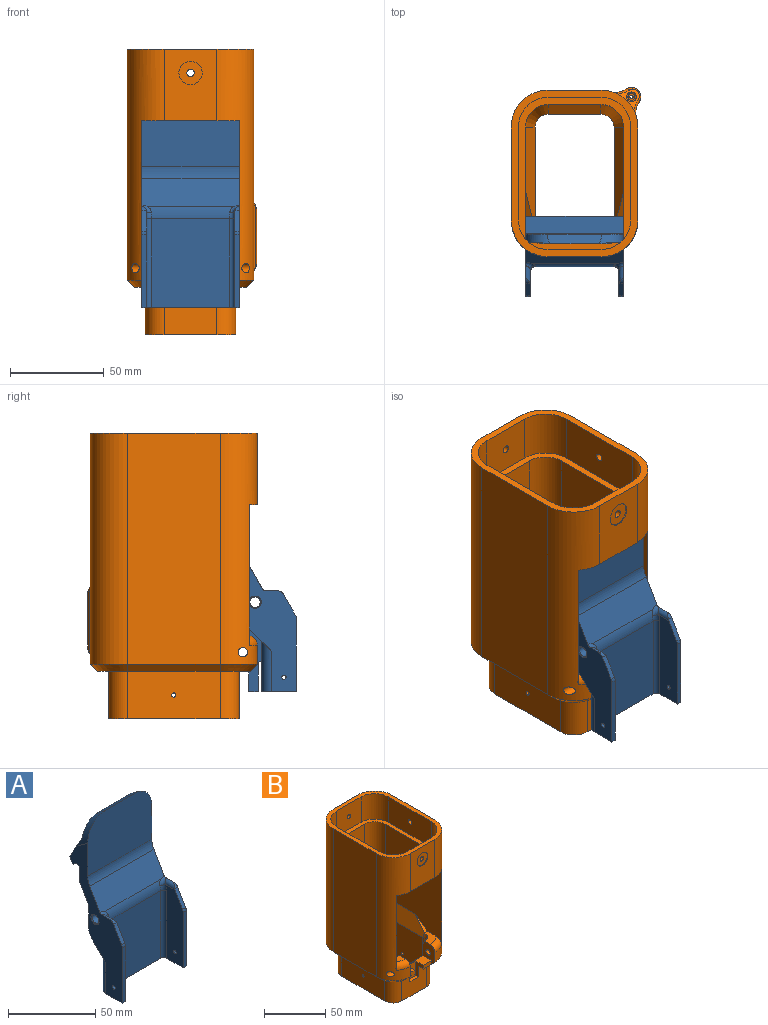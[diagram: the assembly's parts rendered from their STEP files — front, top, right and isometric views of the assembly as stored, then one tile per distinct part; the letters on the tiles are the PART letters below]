
ASSEMBLY  parts=2 mates=1
PART A: 74 faces, bbox 55.6x46.3x116.4 mm
  f0: cylinder r=5.71mm len=7.94mm, axis (-1,0,0), area 71.3mm2, adj f1,f14,f40,f43
  f1: plane 25.4x2.96mm, normal (0,1,0), area 48.8mm2, adj f0,f3,f16,f29,f40,f43,f44,f73
  f2: plane 25.4x4.95mm, normal (0,0,-1), area 110.7mm2, adj f3,f13,f23,f40,f43,f44,f46,f62
  f3: plane 39.51x15.88mm, normal (1,0,0), area 282.7mm2, adj f1,f2,f16,f23,f24,f25,f26,f27
  f4: plane 98.14x42.62mm, normal (1,0,0), area 1360.4mm2, adj f7,f17,f18,f22,f28,f30,f31,f32
  f5: plane 98.14x42.62mm, normal (-1,0,0), area 1360.4mm2, adj f8,f10,f17,f18,f22,f28,f30,f31
  f6: plane 51.21x13.82mm, normal (-1,0,0), area 642.1mm2, adj f7,f17,f49,f50,f51,f59,f61,f67
  f7: cylinder r=2.54mm len=9.64mm, axis (0,1,0), area 26.8mm2, adj f4,f6,f52,f60,f61
  f8: plane 38.82x2.54mm, normal (0,-1,0), area 98.6mm2, adj f5,f9,f17,f58
  f9: plane 51.21x13.82mm, normal (1,0,0), area 642.1mm2, adj f8,f10,f17,f53,f54,f56,f58,f66
  f10: cylinder r=2.54mm len=9.64mm, axis (0,-1,0), area 26.8mm2, adj f5,f9,f55,f56,f57
  f11: plane 47.4x41.91mm, normal (0,-1,0), area 1986.4mm2, adj f12,f17,f50,f53
  f12: cylinder r=12.7mm len=45.35mm, axis (-1,0,0), area 284.6mm2, adj f11,f30,f51,f52,f54,f55
  f13: plane 12.07x7.94mm, normal (0,1,0), area 95.8mm2, adj f2,f14,f40,f43
  f14: cylinder r=3.17mm len=7.94mm, axis (-1,0,0), area 39.6mm2, adj f0,f13,f40,f43
  f15: cylinder r=2.6mm len=7.94mm, axis (-1,0,0), area 129.8mm2, adj f40,f43
  f16: cylinder r=5.71mm len=7.94mm, axis (-1,0,0), area 71.3mm2, adj f1,f3,f24,f44
  f17: plane 52.07x18.42mm, normal (0,0,-1), area 204.6mm2, adj f4,f5,f6,f8,f9,f11,f38,f49
  f18: plane 52.1x15.43mm, normal (0,0.87,0.5), area 925.3mm2, adj f4,f5,f19,f36,f41,f42
  f19: cylinder r=5.08mm len=51.58mm, axis (-1,0,0), area 136mm2, adj f18,f20,f41,f42
  f20: plane 52.71x12.86mm, normal (0,1,0), area 478.1mm2, adj f19,f21,f41,f42
  f21: plane 29.57x5.08mm, normal (0,0.59,0.81), area 177mm2, adj f20,f22,f41,f42
  f22: plane 52.07x39.2mm, normal (0,-1,0), area 1948.5mm2, adj f4,f5,f21,f41,f42,f47
  f23: plane 12.07x7.94mm, normal (0,1,0), area 95.8mm2, adj f2,f3,f24,f44
  f24: cylinder r=3.17mm len=7.94mm, axis (-1,0,0), area 39.6mm2, adj f3,f16,f23,f44
  f25: plane 25.4x5.62mm, normal (0,0.64,0.77), area 186.5mm2, adj f3,f26,f29,f40
  f26: cylinder r=0.64mm len=25.4mm, axis (-1,0,0), area 14.1mm2, adj f3,f25,f28,f40
  f27: cylinder r=2.6mm len=7.94mm, axis (-1,0,0), area 129.8mm2, adj f3,f44
  f28: plane 52.07x23.8mm, normal (0,1,0), area 1027.3mm2, adj f3,f4,f5,f26,f31,f40,f70,f71
  f29: cylinder r=3.17mm len=25.4mm, axis (-1,0,0), area 70.4mm2, adj f1,f3,f25,f40
  f30: plane 52.23x15.16mm, normal (0,-0.87,0.5), area 898mm2, adj f4,f5,f12,f47,f52,f55
  f31: plane 52.07x12.1mm, normal (0,0.87,-0.5), area 727.4mm2, adj f4,f5,f28,f32
  f32: plane 52.07x9.48mm, normal (0,1,0), area 493.6mm2, adj f4,f5,f31,f33
  f33: cylinder r=2.54mm len=52.07mm, axis (-1,0,0), area 346.3mm2, adj f4,f5,f32,f34
  f34: plane 52.07x0.13mm, normal (0,-0.87,-0.5), area 7.6mm2, adj f4,f5,f33,f35
  f35: cylinder r=0.76mm len=52.07mm, axis (-1,0,0), area 83.1mm2, adj f4,f5,f34,f36
  f36: plane 52.07x3.76mm, normal (0,0.87,-0.5), area 226.2mm2, adj f4,f5,f18,f35
  f37: plane 15.47x13.32mm, normal (0,0.71,-0.71), area 122.9mm2, adj f3,f4,f38,f64,f71
  f38: plane 41.91x26.67mm, normal (0,1,0), area 817.7mm2, adj f3,f17,f37,f39,f40,f63,f64,f65
  f39: plane 15.47x13.32mm, normal (0,0.71,-0.71), area 122.9mm2, adj f5,f38,f40,f63,f70
  f40: plane 39.51x15.88mm, normal (-1,0,0), area 282.7mm2, adj f0,f1,f2,f13,f14,f15,f25,f26
  f41: cylinder r=13.33mm len=23.82mm, axis (0,-0.82,0.57), area 137.7mm2, adj f4,f18,f19,f20,f21,f22
  f42: cylinder r=13.33mm len=23.82mm, axis (0,-0.82,0.57), area 137.7mm2, adj f5,f18,f19,f20,f21,f22
  f43: plane 25.72x10.48mm, normal (1,0,0), area 96.4mm2, adj f0,f1,f2,f13,f14,f15,f45,f46
  f44: plane 25.72x10.48mm, normal (-1,0,0), area 96.4mm2, adj f1,f2,f16,f23,f24,f27,f45,f46
  f45: cylinder r=4.76mm len=9.53mm, axis (1,0,0), area 102.9mm2, adj f43,f44,f46,f72
  f46: plane 20.96x9.53mm, normal (0,1,0), area 199.6mm2, adj f2,f43,f44,f45
  f47: cylinder r=12.7mm len=52.07mm, axis (-1,0,0), area 346.3mm2, adj f4,f5,f22,f30
  f48: cylinder r=2.78mm len=51.05mm, axis (1,0,0), area 891.3mm2, adj f68,f69
  f49: plane 38.82x2.54mm, normal (0,-1,0), area 98.6mm2, adj f4,f6,f17,f59
  f50: cylinder r=2.54mm len=47.4mm, axis (0,0,1), area 189.1mm2, adj f6,f11,f17,f51
  f51: torus R=15.24mm, axis (1,0,0), area 13.7mm2, adj f6,f12,f50,f52
  f52: bspline ~5.75x5.23mm, area 17.1mm2, adj f4,f7,f12,f30,f51
  f53: cylinder r=2.54mm len=47.4mm, axis (0,0,1), area 189.1mm2, adj f9,f11,f17,f54
  f54: torus R=15.24mm, axis (-1,0,0), area 13.7mm2, adj f9,f12,f53,f55
  f55: bspline ~5.75x5.23mm, area 17.1mm2, adj f5,f10,f12,f30,f54
  f56: plane 11.12x6.42mm, normal (0,-0.87,0.5), area 32.6mm2, adj f5,f9,f10,f57,f58
  f57: cylinder r=3.81mm len=3.3mm, axis (1,0,0), area 4.9mm2, adj f5,f10,f56
  f58: cylinder r=3.81mm len=2.54mm, axis (1,0,0), area 5.1mm2, adj f5,f8,f9,f56
  f59: cylinder r=3.81mm len=2.54mm, axis (1,0,0), area 5.1mm2, adj f4,f6,f49,f61
  f60: cylinder r=3.81mm len=3.3mm, axis (1,0,0), area 4.9mm2, adj f4,f7,f61
  f61: plane 11.12x6.42mm, normal (0,-0.87,0.5), area 32.6mm2, adj f4,f6,f7,f59,f60
  f62: plane 25.4x14.86mm, normal (0,-1,0), area 377.4mm2, adj f2,f3,f40,f65
  f63: cylinder r=5.08mm len=26.67mm, axis (0,0,-1), area 192.5mm2, adj f5,f17,f38,f39
  f64: cylinder r=5.08mm len=26.67mm, axis (0,0,1), area 192.5mm2, adj f4,f17,f37,f38
  f65: cylinder r=1.02mm len=25.4mm, axis (1,0,0), area 81.1mm2, adj f3,f38,f40,f62
  f66: cylinder r=1.13mm len=2.54mm, axis (1,0,0), area 18mm2, adj f5,f9
  f67: cylinder r=1.13mm len=2.54mm, axis (1,0,0), area 18mm2, adj f4,f6
  f68: cone r=2.78mm half-angle=45deg, axis (-1,0,0), area 13.7mm2, adj f5,f48
  f69: cone r=2.78mm half-angle=45deg, axis (1,0,0), area 13.7mm2, adj f4,f48
  f70: cylinder r=9.53mm len=13.34mm, axis (-1,0,0), area 99.8mm2, adj f5,f28,f39,f40
  f71: cylinder r=9.53mm len=13.34mm, axis (-1,0,0), area 99.8mm2, adj f3,f4,f28,f37
  f72: plane 9.53x1.61mm, normal (0,-0.64,-0.77), area 20mm2, adj f43,f44,f45,f73
  f73: cylinder r=0.64mm len=9.53mm, axis (-1,0,0), area 13.7mm2, adj f1,f43,f44,f72
PART B: 104 faces, bbox 75.7x98.6x155.2 mm
  f0: cylinder r=19.69mm len=123.19mm, axis (0,0,-1), area 2900mm2, adj f14,f17,f26,f59,f77,f79,f84,f85
  f1: plane 28.19x9.65mm, normal (0,0,1), area 190.5mm2, adj f4,f36,f66,f67,f68,f73,f74,f75
  f2: plane 28.19x25.4mm, normal (0,-1,0), area 613.3mm2, adj f3,f27,f48,f54,f74,f75,f76
  f3: plane 81.28x59.94mm, normal (0,0,-1), area 1328mm2, adj f2,f4,f48,f49,f50,f51,f52,f53
  f4: plane 9.33x3.81mm, normal (0,-1,0), area 35.6mm2, adj f1,f3,f66,f74
  f5: plane 52.32x7.62mm, normal (0,0,-1), area 367mm2, adj f10,f11,f12,f13,f29,f30
  f6: plane 75.72x59.94mm, normal (0,0,1), area 705.9mm2, adj f18,f19,f20,f22,f23,f24,f25,f28
  f7: plane 48.83x3.81mm, normal (0,0,1), area 161.2mm2, adj f13,f20,f21,f22
  f8: plane 15.37x12.07mm, normal (0,0,1), area 107.5mm2, adj f29,f41,f63,f66,f71
  f9: cylinder r=2.5mm len=17.21mm, axis (1,0,0), area 241.7mm2, adj f11,f67
  f10: cylinder r=19.69mm len=123.19mm, axis (0,0,-1), area 2811mm2, adj f5,f12,f16,f26,f29,f56,f65,f66
  f11: cylinder r=19.69mm len=123.19mm, axis (0,0,-1), area 2811mm2, adj f5,f9,f12,f17,f26,f30,f55,f67
  f12: plane 38.1x28.19mm, normal (0,-1,0), area 952.5mm2, adj f5,f10,f11,f26,f97
  f13: plane 52.32x12.7mm, normal (0,1,0), area 664.5mm2, adj f5,f7,f29,f30,f69,f70
  f14: plane 123.19x28.19mm, normal (0,1,0), area 3351.6mm2, adj f0,f15,f26,f61,f100
  f15: cylinder r=19.69mm len=123.19mm, axis (0,0,-1), area 3809.2mm2, adj f14,f16,f26,f60
  f16: plane 123.19x49.53mm, normal (-1,0,0), area 6101.6mm2, adj f10,f15,f26,f58
  f17: plane 123.19x49.53mm, normal (1,0,0), area 5979.9mm2, adj f0,f11,f26,f57,f92
  f18: cylinder r=15.88mm len=25.4mm, axis (0,0,-1), area 633.4mm2, adj f6,f19,f25,f26
  f19: plane 49.53x25.4mm, normal (-1,0,0), area 1245.7mm2, adj f6,f18,f20,f26,f94
  f20: cylinder r=15.88mm len=25.4mm, axis (0,0,-1), area 633.4mm2, adj f6,f7,f19,f21,f26,f70
  f21: plane 28.19x25.4mm, normal (0,1,0), area 703.8mm2, adj f7,f20,f22,f26,f95
  f22: cylinder r=15.88mm len=25.4mm, axis (0,0,-1), area 633.4mm2, adj f6,f7,f21,f23,f26,f69
  f23: plane 49.53x25.4mm, normal (1,0,0), area 1258.1mm2, adj f6,f22,f24,f26
  f24: cylinder r=15.88mm len=25.4mm, axis (0,0,-1), area 633.4mm2, adj f6,f23,f25,f26
  f25: plane 28.19x25.4mm, normal (0,-1,0), area 703.8mm2, adj f6,f18,f24,f26,f98
  f26: plane 88.9x67.56mm, normal (0,0,1), area 1017.9mm2, adj f0,f10,f11,f12,f14,f15,f16,f17
  f27: plane 69.6x48.26mm, normal (0,0,-1), area 668.9mm2, adj f2,f33,f34,f35,f36,f37,f38,f39
  f28: cylinder r=12.06mm len=72.4mm, axis (0,0,1), area 1372.2mm2, adj f6,f29,f32,f45
  f29: plane 90.39x67.85mm, normal (1,0,0), area 4914.4mm2, adj f5,f6,f8,f10,f13,f28,f43,f63
  f30: plane 90.39x67.85mm, normal (-1,0,0), area 4914.4mm2, adj f5,f6,f11,f13,f31,f44,f62,f64
  f31: cylinder r=12.06mm len=72.4mm, axis (0,0,1), area 1372.2mm2, adj f6,f30,f32,f46
  f32: plane 72.4x28.19mm, normal (0,-1,0), area 2041.3mm2, adj f6,f28,f31,f47
  f33: cylinder r=6.99mm len=40.64mm, axis (0,0,-1), area 445.9mm2, adj f27,f34,f38,f46
  f34: plane 48.77x40.64mm, normal (-1,0,0), area 1977.9mm2, adj f27,f33,f35,f44,f102
  f35: cylinder r=6.99mm len=40.64mm, axis (0,0,-1), area 445.9mm2, adj f27,f34,f36,f42,f67
  f36: plane 29.21x28.19mm, normal (0,1,0), area 823.5mm2, adj f1,f27,f35,f37
  f37: cylinder r=6.99mm len=40.64mm, axis (0,0,-1), area 445.9mm2, adj f27,f36,f39,f41,f66
  f38: plane 40.64x28.19mm, normal (0,-1,0), area 1141.8mm2, adj f27,f33,f40,f47,f103
  f39: plane 48.77x40.64mm, normal (1,0,0), area 1977.9mm2, adj f27,f37,f40,f43,f101
  f40: cylinder r=6.99mm len=40.64mm, axis (0,0,-1), area 445.9mm2, adj f27,f38,f39,f45
  f41: cone r=6.99mm half-angle=20deg, axis (0,0,1), area 48.9mm2, adj f8,f37,f43,f66
  f42: cone r=6.99mm half-angle=20deg, axis (0,0,1), area 48.9mm2, adj f35,f44,f62,f67
  f43: plane 48.77x13.96mm, normal (0.94,0,0.34), area 646.1mm2, adj f29,f39,f41,f45,f63
  f44: plane 48.77x13.96mm, normal (-0.94,0,0.34), area 646.1mm2, adj f30,f34,f42,f46,f64
  f45: cone r=15.31mm half-angle=20deg, axis (0,0,1), area 222.2mm2, adj f28,f40,f43,f47
  f46: cone r=15.31mm half-angle=20deg, axis (0,0,1), area 222.2mm2, adj f31,f33,f44,f47
  f47: plane 28.19x13.96mm, normal (0,-0.94,0.34), area 418.8mm2, adj f32,f38,f45,f46
  f48: cylinder r=10.03mm len=25.4mm, axis (0,0,-1), area 400.3mm2, adj f2,f3,f27,f49
  f49: plane 49.53x25.4mm, normal (1,0,0), area 1254mm2, adj f3,f27,f48,f50,f102
  f50: cylinder r=10.03mm len=25.4mm, axis (0,0,-1), area 400.3mm2, adj f3,f27,f49,f51
  f51: plane 28.19x25.4mm, normal (0,1,0), area 712.1mm2, adj f3,f27,f50,f52,f103
  f52: cylinder r=10.03mm len=25.4mm, axis (0,0,-1), area 400.3mm2, adj f3,f27,f51,f53
  f53: plane 49.53x25.4mm, normal (-1,0,0), area 1254mm2, adj f3,f27,f52,f54,f101
  f54: cylinder r=10.03mm len=25.4mm, axis (0,0,-1), area 400.3mm2, adj f2,f3,f27,f53
  f55: cone r=19.69mm half-angle=45deg, axis (0,0,1), area 150.5mm2, adj f3,f11,f57,f67
  f56: cone r=19.69mm half-angle=45deg, axis (0,0,1), area 150.5mm2, adj f3,f10,f58,f66
  f57: plane 49.53x3.81mm, normal (0.71,0,-0.71), area 266.9mm2, adj f3,f17,f55,f59
  f58: plane 49.53x3.81mm, normal (-0.71,0,-0.71), area 266.9mm2, adj f3,f16,f56,f60
  f59: cone r=19.69mm half-angle=45deg, axis (0,0,1), area 150.5mm2, adj f0,f3,f57,f61
  f60: cone r=19.69mm half-angle=45deg, axis (0,0,1), area 150.5mm2, adj f3,f15,f58,f61
  f61: plane 28.19x3.81mm, normal (0,0.71,-0.71), area 151.9mm2, adj f3,f14,f59,f60
  f62: plane 15.37x12.07mm, normal (0,0,1), area 107.5mm2, adj f30,f42,f64,f67,f72
  f63: plane 14.49x10.15mm, normal (0,-0.57,0.82), area 32.7mm2, adj f8,f29,f43
  f64: plane 14.49x10.15mm, normal (0,-0.57,0.82), area 32.7mm2, adj f30,f44,f62
  f65: cylinder r=2.5mm len=17.21mm, axis (1,0,0), area 241.8mm2, adj f10,f66
  f66: plane 19.05x13.46mm, normal (1,0,0), area 184.6mm2, adj f1,f4,f8,f10,f37,f41,f56,f65
  f67: plane 19.05x13.46mm, normal (-1,0,0), area 184.6mm2, adj f1,f9,f11,f35,f42,f55,f62,f68
  f68: plane 9.33x3.81mm, normal (0,-1,0), area 35.6mm2, adj f1,f3,f67,f75
  f69: plane 1.75x1.75mm, normal (0,0,-1), area 1.4mm2, adj f13,f22,f29
  f70: plane 1.75x1.75mm, normal (0,0,-1), area 1.4mm2, adj f13,f20,f30
  f71: torus R=14.61mm, axis (0,0,-1), area 115mm2, adj f8,f10,f29,f66
  f72: torus R=14.61mm, axis (0,0,-1), area 115mm2, adj f11,f30,f62,f67
  f73: plane 14.61x9.53mm, normal (0,-1,0), area 139.1mm2, adj f1,f74,f75,f76
  f74: plane 14.61x8.57mm, normal (1,0,0), area 62.1mm2, adj f1,f2,f3,f4,f73,f76
  f75: plane 14.61x8.57mm, normal (-1,0,0), area 62.1mm2, adj f1,f2,f3,f68,f73,f76
  f76: plane 9.53x2.73mm, normal (0,0,1), area 26mm2, adj f2,f73,f74,f75
  f77: cylinder r=9.53mm len=43.87mm, axis (0,0,1), area 320.5mm2, adj f0,f78,f86,f89
  f78: cylinder r=5mm len=32.25mm, axis (0,0,1), area 450.2mm2, adj f77,f79,f87,f90
  f79: cylinder r=9.53mm len=43.87mm, axis (0,0,1), area 320.5mm2, adj f0,f78,f88,f91
  f80: cylinder r=2.6mm len=29.83mm, axis (0,0,1), area 446.5mm2, adj f82,f84
  f81: plane 3.68x3.68mm, normal (0,0,1), area 8.2mm2, adj f82,f83
  f82: torus R=1.84mm, axis (0,0,1), area 17.5mm2, adj f80,f81
  f83: cylinder r=0.89mm len=11.73mm, axis (0,0,1), area 60.6mm2, adj f81,f85
  f84: cone r=19.69mm half-angle=45deg, axis (0,0,-1), area 72.5mm2, adj f0,f80,f89,f90,f91
  f85: cone r=28.07mm half-angle=45deg, axis (0,0,1), area 83.1mm2, adj f0,f83,f86,f87,f88
  f86: bspline ~12.3x8.82mm, area 18.8mm2, adj f0,f77,f85,f87
  f87: bspline ~8.52x8.08mm, area 23.2mm2, adj f78,f85,f86,f88
  f88: bspline ~12.3x8.82mm, area 18.8mm2, adj f0,f79,f85,f87
  f89: bspline ~12.3x8.82mm, area 18.8mm2, adj f0,f77,f84,f90
  f90: bspline ~8.52x8.52mm, area 23.2mm2, adj f78,f84,f89,f91
  f91: bspline ~12.3x8.82mm, area 18.8mm2, adj f0,f79,f84,f90
  f92: cylinder r=6.22mm len=12.45mm, axis (-1,0,0), area 24.8mm2, adj f17,f93
  f93: plane 12.45x12.45mm, normal (1,0,0), area 109.3mm2, adj f92,f94
  f94: cylinder r=1.98mm len=3.97mm, axis (-1,0,0), area 39.6mm2, adj f19,f93
  f95: cylinder r=1.98mm len=3.97mm, axis (0,1,0), area 39.6mm2, adj f21,f96
  f96: plane 12.45x12.45mm, normal (0,-1,0), area 109.3mm2, adj f95,f97
  f97: cylinder r=6.22mm len=12.45mm, axis (0,1,0), area 24.8mm2, adj f12,f96
  f98: cylinder r=1.98mm len=3.97mm, axis (0,-1,0), area 39.6mm2, adj f25,f99
  f99: plane 12.45x12.45mm, normal (0,1,0), area 109.3mm2, adj f98,f100
  f100: cylinder r=6.22mm len=12.45mm, axis (0,-1,0), area 24.8mm2, adj f14,f99
  f101: cylinder r=1.13mm len=3.05mm, axis (1,0,0), area 21.6mm2, adj f39,f53
  f102: cylinder r=1.13mm len=3.05mm, axis (1,0,0), area 21.6mm2, adj f34,f49
  f103: cylinder r=1.13mm len=3.05mm, axis (0,1,0), area 21.6mm2, adj f38,f51
PLACE A rot(axis=(0.96,-0.29,-0.01),0deg) t=(-22.59,-20.64,-15.5)mm
PLACE B t=(-22.59,-20.64,-15.5)mm fixed
MATE revolute A.f0 <-> B.f9  axis (1,0,0) through (-22.59,-57.47,-56.14)mm
